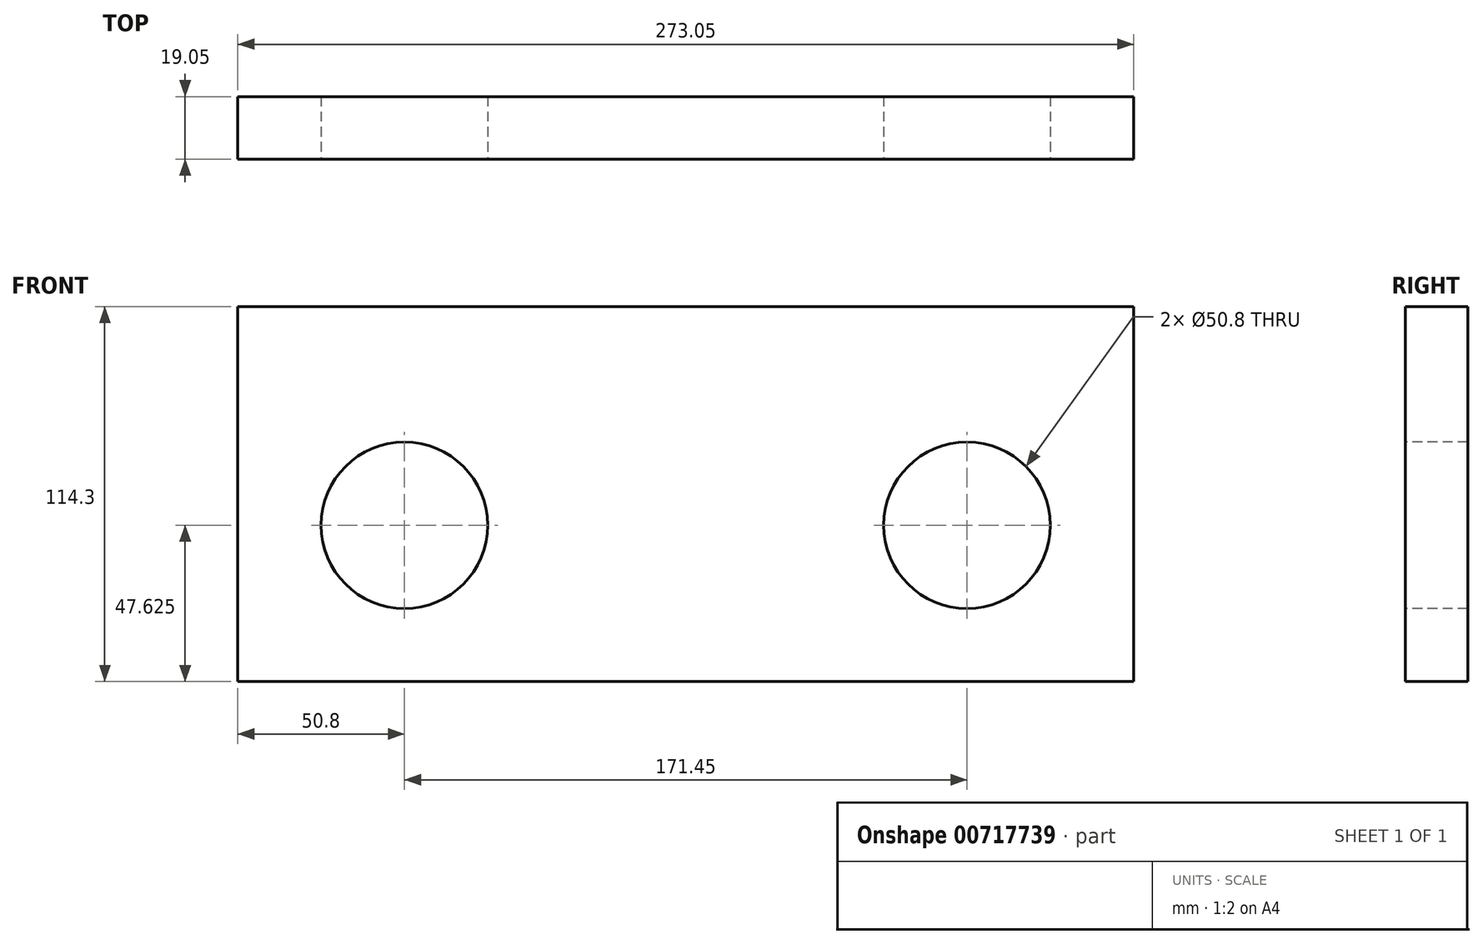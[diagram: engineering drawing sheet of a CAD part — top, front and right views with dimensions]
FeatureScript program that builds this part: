
annotation { "Feature Type Name" : "Feature", "Feature Type Description" : "" }
export const myFeature = defineFeature(function(context is Context, id is Id, definition is map)
    precondition{}
    {
        {
            var Q0;
            Q0=qCreatedBy(makeId("Front.planeOp"),FACE);
            var sketch = newSketch(context, id + "F0", { "sketchPlane" : qUnion([Q0])});
            skLineSegment(sketch, "E0.bottom", {"start": v(0, 0) * mm, "end": v(273.05, 0) * mm});
            skLineSegment(sketch, "E0.top", {"start": v(0, 114.3) * mm, "end": v(273.05, 114.3) * mm});
            skLineSegment(sketch, "E0.left", {"start": v(0, 0) * mm, "end": v(0, 114.3) * mm});
            skLineSegment(sketch, "E0.right", {"start": v(273.05, 0) * mm, "end": v(273.05, 114.3) * mm});
            skSolve(sketch);
        }
        {
            var Q0;
            Q0=makeQuery(id+"F0.imprint","IMPRINT",FACE,{"disambiguationData":[TD([[makeQuery(id+"F0.imprint","IMPRINT",EDGE,{"derivedFrom":sQuery(id+"F0.wireOp",EDGE,"E0.bottom")}),1.0]])]});
            extrude(context, id + "F1", {"entities" : qUnion([Q0]), "depth" : 19.05 * mm, "offsetDistance" : 25.4 * mm});
        }
        {
            var Q0;
            Q0=makeQuery(id+"F1.opExtrude","CAP_FACE",FACE,{"disambiguationData":[OSD([sQuery(id+"F0.wireOp",EDGE,"E0.bottom"),sQuery(id+"F0.wireOp",EDGE,"E0.top"),sQuery(id+"F0.wireOp",EDGE,"E0.left"),sQuery(id+"F0.wireOp",EDGE,"E0.right")])],"isStart":false});
            var sketch = newSketch(context, id + "F2", { "sketchPlane" : qUnion([Q0])});
            skCircle(sketch, "E1", {"center": v(50.8, 47.63) * mm, "radius": 25.4 * mm});
            skCircle(sketch, "E2", {"center": v(222.25, 47.63) * mm, "radius": 25.4 * mm});
            skSolve(sketch);
        }
        {
            var Q0;
            Q0 = qSketchRegion(id + "F3U8X73pEVCCaN3_1", true);
            var Q1;
            Q1=makeQuery(id+"F2.imprint","IMPRINT",FACE,{"disambiguationData":[TD([[makeQuery(id+"F2.imprint","IMPRINT",EDGE,{"derivedFrom":sQuery(id+"F2.wireOp",EDGE,"E1")}),1.0]])]});
            var Q2;
            Q2=makeQuery(id+"F2.imprint","IMPRINT",FACE,{"disambiguationData":[TD([[makeQuery(id+"F2.imprint","IMPRINT",EDGE,{"derivedFrom":sQuery(id+"F2.wireOp",EDGE,"E2")}),1.0]])]});
            extrude(context, id + "F3", {"entities" : qUnion([Q0, Q1, Q2]), "operationType" : NewBodyOperationType.REMOVE, "oppositeDirection" : true, "depth" : 25.4 * mm, "offsetDistance" : 25.4 * mm});
        }
    });
